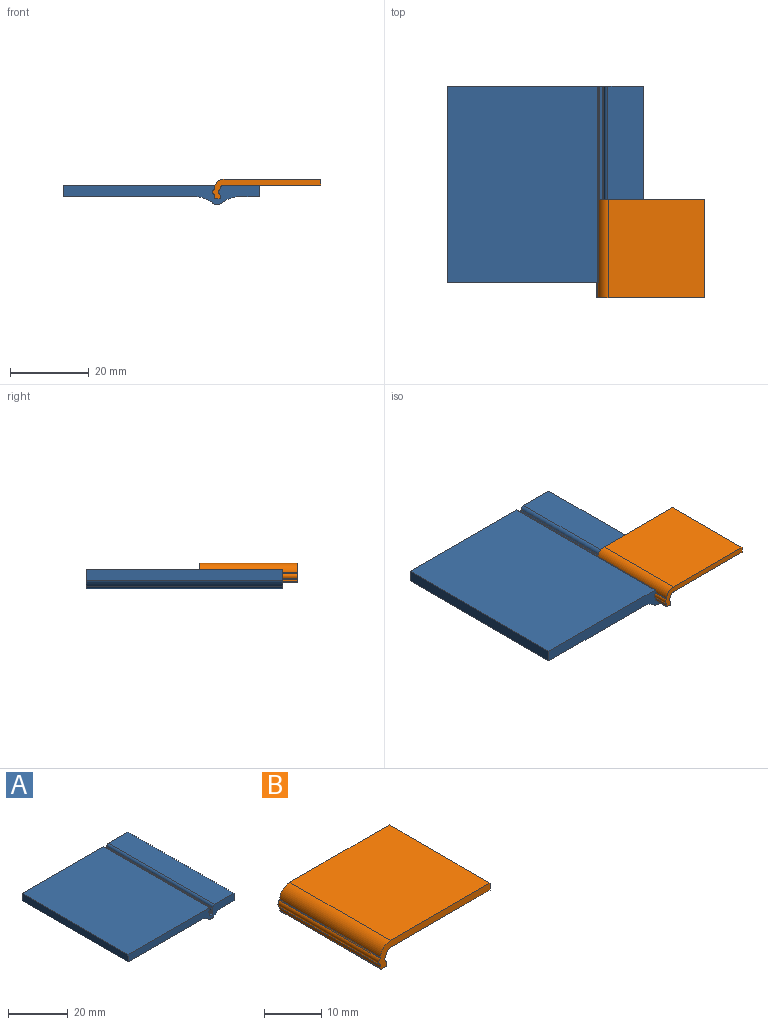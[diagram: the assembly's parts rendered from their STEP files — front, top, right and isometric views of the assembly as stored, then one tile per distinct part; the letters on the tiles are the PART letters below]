
ASSEMBLY  parts=2 mates=2
PART A: 26 faces, bbox 50x50x5 mm
  f0: plane 50x1mm, normal (0,0,1), area 50mm2, adj f14,f15,f20,f22
  f1: plane 50x0.52mm, normal (1,0,0), area 25.9mm2, adj f14,f15,f16,f20
  f2: cylinder r=0.9mm len=50mm, axis (0,1,0), area 69.8mm2, adj f14,f15,f16,f17
  f3: plane 50x0.52mm, normal (1,0,0), area 25.9mm2, adj f14,f15,f17,f21
  f4: plane 50x38.25mm, normal (0,0,1), area 1912.5mm2, adj f5,f14,f15,f21
  f5: plane 50x3mm, normal (-1,0,0), area 150mm2, adj f4,f6,f14,f15
  f6: plane 50x34.03mm, normal (0,0,-1), area 1701.4mm2, adj f5,f7,f14,f15
  f7: cylinder r=6mm len=50mm, axis (0,1,0), area 216.8mm2, adj f6,f14,f15,f25
  f8: cylinder r=6mm len=50mm, axis (0,1,0), area 216.8mm2, adj f9,f14,f15,f24
  f9: plane 50x5.53mm, normal (0,0,-1), area 276.4mm2, adj f8,f10,f14,f15
  f10: plane 50x3mm, normal (1,0,0), area 150mm2, adj f9,f11,f14,f15
  f11: plane 50x9.02mm, normal (0,0,1), area 450.9mm2, adj f10,f14,f15,f23
  f12: cylinder r=0.9mm len=50mm, axis (0,1,0), area 69.8mm2, adj f14,f15,f18,f19
  f13: plane 50x0.52mm, normal (-1,0,0), area 25.9mm2, adj f14,f15,f19,f22
  f14: plane 50x5mm, normal (0,-1,0), area 152.9mm2, adj f0,f1,f2,f3,f4,f5,f6,f7
  f15: plane 50x5mm, normal (0,1,0), area 152.9mm2, adj f0,f1,f2,f3,f4,f5,f6,f7
  f16: cylinder r=0.5mm len=50mm, axis (0,1,0), area 19.4mm2, adj f1,f2,f14,f15
  f17: cylinder r=0.5mm len=50mm, axis (0,1,0), area 19.4mm2, adj f2,f3,f14,f15
  f18: cylinder r=0.5mm len=50mm, axis (0,1,0), area 15.5mm2, adj f12,f14,f15,f23
  f19: cylinder r=0.5mm len=50mm, axis (0,1,0), area 19.4mm2, adj f12,f13,f14,f15
  f20: cylinder r=0.25mm len=50mm, axis (0,-1,0), area 19.6mm2, adj f0,f1,f14,f15
  f21: cylinder r=0.25mm len=50mm, axis (0,1,0), area 19.6mm2, adj f3,f4,f14,f15
  f22: cylinder r=0.25mm len=50mm, axis (0,1,0), area 19.6mm2, adj f0,f13,f14,f15
  f23: cylinder r=1mm len=50mm, axis (0,1,0), area 70.8mm2, adj f11,f14,f15,f18
  f24: cylinder r=2mm len=50mm, axis (0,1,0), area 68.8mm2, adj f8,f14,f15,f25
  f25: cylinder r=2mm len=50mm, axis (0,1,0), area 68.8mm2, adj f7,f14,f15,f24
PART B: 18 faces, bbox 27.6x25x5 mm
  f0: plane 25x1.5mm, normal (1,0,0), area 37.5mm2, adj f1,f9,f10,f11
  f1: plane 25x24.68mm, normal (0,0,1), area 617.1mm2, adj f0,f2,f10,f11
  f2: cylinder r=2.5mm len=25mm, axis (0,1,0), area 95.3mm2, adj f1,f10,f11,f12
  f3: cylinder r=0.9mm len=25mm, axis (0,1,0), area 38.8mm2, adj f10,f11,f12,f13
  f4: plane 25x0.63mm, normal (-1,0,0), area 15.7mm2, adj f10,f11,f13,f14
  f5: plane 25x1mm, normal (0,0,-1), area 25mm2, adj f10,f11,f14,f15
  f6: plane 25x0.63mm, normal (1,0,0), area 15.7mm2, adj f10,f11,f15,f16
  f7: cylinder r=0.9mm len=25mm, axis (0,1,0), area 38.9mm2, adj f10,f11,f16,f17
  f8: cylinder r=1mm len=25mm, axis (0,1,0), area 36.7mm2, adj f9,f10,f11,f17
  f9: plane 25x24.68mm, normal (0,0,-1), area 617.1mm2, adj f0,f8,f10,f11
  f10: plane 27.58x5mm, normal (0,-1,0), area 44.9mm2, adj f0,f1,f2,f3,f4,f5,f6,f7
  f11: plane 27.58x5mm, normal (0,1,0), area 44.9mm2, adj f0,f1,f2,f3,f4,f5,f6,f7
  f12: cylinder r=0.25mm len=25mm, axis (0,-1,0), area 5.1mm2, adj f2,f3,f10,f11
  f13: cylinder r=0.25mm len=25mm, axis (0,1,0), area 5.4mm2, adj f3,f4,f10,f11
  f14: cylinder r=0.25mm len=25mm, axis (0,-1,0), area 9.8mm2, adj f4,f5,f10,f11
  f15: cylinder r=0.25mm len=25mm, axis (0,-1,0), area 9.8mm2, adj f5,f6,f10,f11
  f16: cylinder r=0.25mm len=25mm, axis (0,1,0), area 5.4mm2, adj f6,f7,f10,f11
  f17: cylinder r=0.25mm len=25mm, axis (0,1,0), area 4.8mm2, adj f7,f8,f10,f11
PLACE A t=(-5.89,24.57,-4.98)mm fixed
PLACE B t=(59.79,-4.33,-1.98)mm
MATE planar B.f6 <-> A.f13  axis (1,0,0) through (34.11,-16.83,-4.92)mm
MATE planar B.f5 <-> A.f0  axis (0,0,-1) through (32.86,-16.83,-5.48)mm
